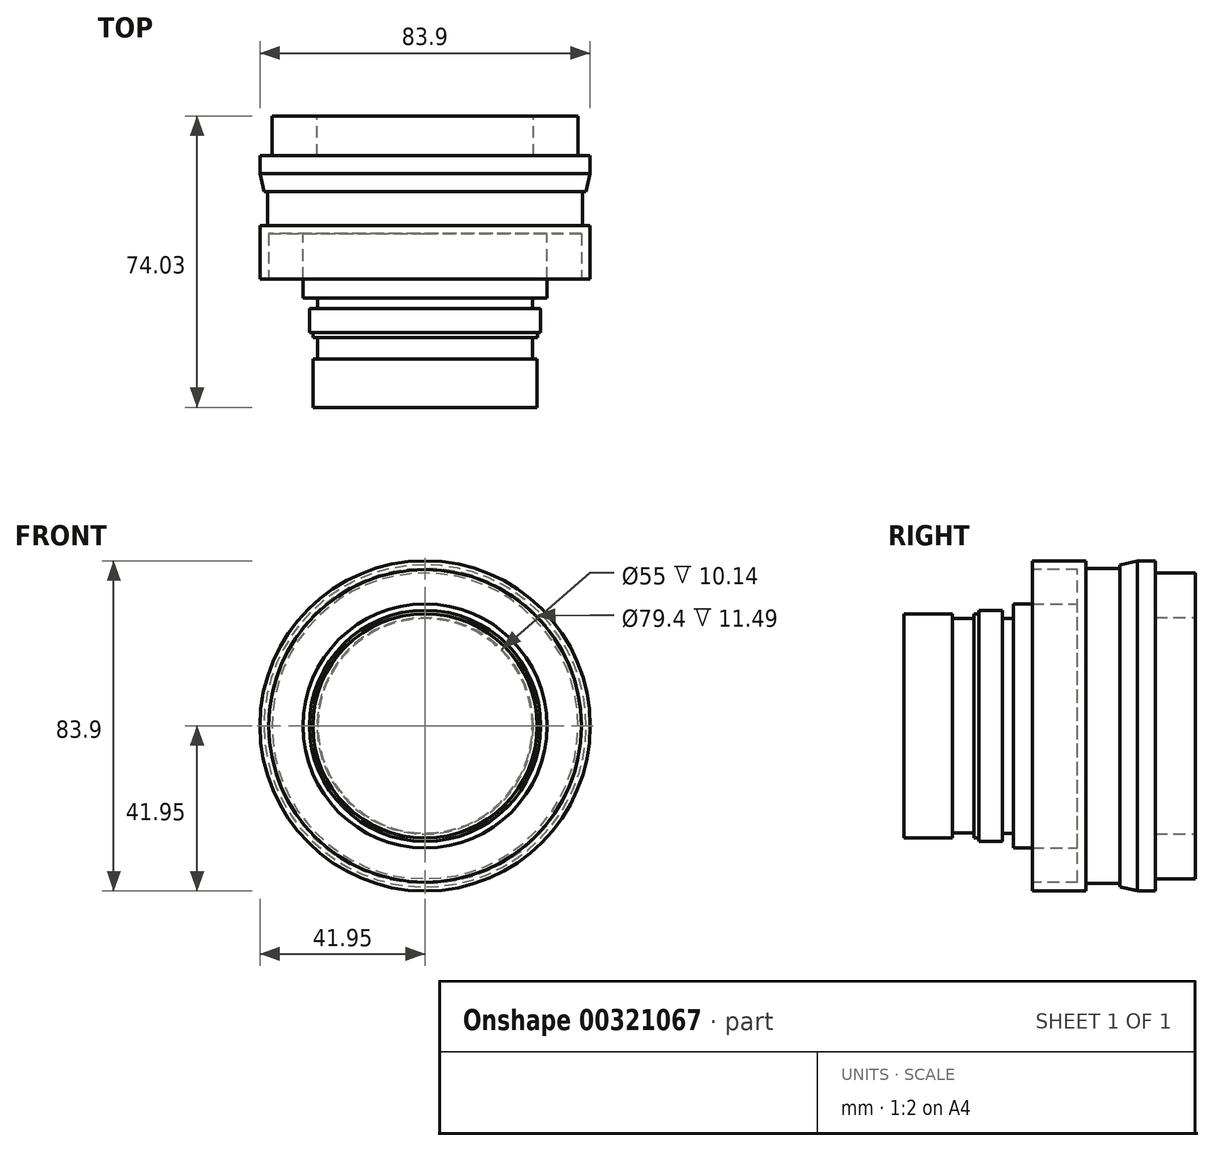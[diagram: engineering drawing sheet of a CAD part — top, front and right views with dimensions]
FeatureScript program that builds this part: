
annotation { "Feature Type Name" : "Feature", "Feature Type Description" : "" }
export const myFeature = defineFeature(function(context is Context, id is Id, definition is map)
    precondition{}
    {
        {
            var Q0;
            Q0=qCreatedBy(makeId("Front.planeOp"),FACE);
            var sketch = newSketch(context, id + "F0", { "sketchPlane" : qUnion([Q0])});
            skCircle(sketch, "E0", {"center": v(0, 0) * mm, "radius": 38.84 * mm});
            skCircle(sketch, "E1", {"center": v(0, 0) * mm, "radius": 27.5 * mm});
            skSolve(sketch);
        }
        {
            var Q0;
            Q0 = qSketchRegion(id + "F0", true);
            extrude(context, id + "F1", {"entities" : qUnion([Q0]), "depth" : 10.14 * mm});
        }
        {
            var Q0;
            Q0=makeQuery(id+"F1.opExtrude","CAP_FACE",FACE,{"disambiguationData":[OSD([sQuery(id+"F0.wireOp",EDGE,"E0"),sQuery(id+"F0.wireOp",EDGE,"E1")])],"isStart":false});
            var sketch = newSketch(context, id + "F2", { "sketchPlane" : qUnion([Q0])});
            skCircle(sketch, "E2", {"center": v(0, 0) * mm, "radius": 41.88 * mm});
            skSolve(sketch);
        }
        {
            var Q0;
            Q0 = qSketchRegion(id + "F2", true);
            extrude(context, id + "F3", {"entities" : qUnion([Q0]), "operationType" : NewBodyOperationType.ADD, "depth" : 4.57 * mm});
        }
        {
            var Q0;
            Q0=makeQuery(id+"F3.opExtrude","CAP_FACE",FACE,{"disambiguationData":[OSD([sQuery(id+"F2.wireOp",EDGE,"E2")])],"isStart":false});
            var sketch = newSketch(context, id + "F4", { "sketchPlane" : qUnion([Q0])});
            skCircle(sketch, "E3", {"center": v(0, 0) * mm, "radius": 41.88 * mm});
            skSolve(sketch);
        }
        {
            var Q0;
            Q0=makeQuery(id+"F4.imprint","IMPRINT",FACE,{"disambiguationData":[TD([[makeQuery(id+"F4.imprint","IMPRINT",EDGE,{"derivedFrom":sQuery(id+"F4.wireOp",EDGE,"E3")}),1.0]])]});
            cPlane(context, id + "F5", {"entities" : qUnion([Q0]), "cplaneType" : CPlaneType.OFFSET, "offset" : 4.5 * mm, "width" : 150 * mm, "height" : 150 * mm});
        }
        {
            var Q0;
            Q0=qCreatedBy(id+"F5.planeOp",FACE);
            var sketch = newSketch(context, id + "F6", { "sketchPlane" : qUnion([Q0])});
            skCircle(sketch, "E4", {"center": v(0, 0) * mm, "radius": 40.92 * mm});
            skSolve(sketch);
        }
        {
            var Q1;
            Q1 = qSketchRegion(id + "F4", true);
            var Q2;
            Q2 = qSketchRegion(id + "F6", true);
            loft(context, id + "F7", {"operationType" : NewBodyOperationType.ADD, "sheetProfilesArray" : [{ "sheetProfileEntities" : qUnion([Q1]) }, { "sheetProfileEntities" : qUnion([Q2]) }]});
        }
        {
            var Q0;
            Q0=makeQuery(id+"F7.opLoft","CAP_FACE",FACE,{"disambiguationData":[OSD([makeQuery(id+"F6.imprint","IMPRINT",FACE,{"disambiguationData":[TD([[makeQuery(id+"F6.imprint","IMPRINT",EDGE,{"derivedFrom":sQuery(id+"F6.wireOp",EDGE,"E4")}),1.0]])]})])],"isStart":true});
            var sketch = newSketch(context, id + "F8", { "sketchPlane" : qUnion([Q0])});
            skCircle(sketch, "E5", {"center": v(0, 0) * mm, "radius": 40 * mm});
            skSolve(sketch);
        }
        {
            var Q0;
            Q0 = qSketchRegion(id + "F8", true);
            extrude(context, id + "F9", {"entities" : qUnion([Q0]), "operationType" : NewBodyOperationType.ADD, "depth" : 8.65 * mm});
        }
        {
            var Q0;
            Q0=makeQuery(id+"F9.opExtrude","CAP_FACE",FACE,{"disambiguationData":[OSD([sQuery(id+"F8.wireOp",EDGE,"E5")])],"isStart":false});
            var sketch = newSketch(context, id + "F10", { "sketchPlane" : qUnion([Q0])});
            skCircle(sketch, "E6", {"center": v(0, 0) * mm, "radius": 41.95 * mm});
            skSolve(sketch);
        }
        {
            var Q0;
            Q0 = qSketchRegion(id + "F10", true);
            extrude(context, id + "F11", {"entities" : qUnion([Q0]), "operationType" : NewBodyOperationType.ADD, "depth" : 13.57 * mm});
        }
        {
            var Q0;
            Q0=makeQuery(id+"F11.opExtrude","CAP_FACE",FACE,{"disambiguationData":[OSD([sQuery(id+"F10.wireOp",EDGE,"E6")])],"isStart":false});
            var sketch = newSketch(context, id + "F12", { "sketchPlane" : qUnion([Q0])});
            skCircle(sketch, "E7", {"center": v(0, 0) * mm, "radius": 39.7 * mm});
            skSolve(sketch);
        }
        {
            var Q0;
            Q0 = qSketchRegion(id + "F12", true);
            extrude(context, id + "F13", {"entities" : qUnion([Q0]), "operationType" : NewBodyOperationType.REMOVE, "oppositeDirection" : true, "depth" : 11.5 * mm});
        }
        {
            var Q0;
            Q0=makeQuery(id+"F13.boolean.opBoolean","COPY",FACE,{"derivedFrom":makeQuery(id+"F13.opExtrude","CAP_FACE",FACE,{"disambiguationData":[OSD([sQuery(id+"F12.wireOp",EDGE,"E7")])],"isStart":false})});
            var sketch = newSketch(context, id + "F14", { "sketchPlane" : qUnion([Q0])});
            skCircle(sketch, "E8", {"center": v(0, 0) * mm, "radius": 31 * mm});
            skSolve(sketch);
        }
        {
            var Q0;
            Q0 = qSketchRegion(id + "F14", true);
            extrude(context, id + "F15", {"entities" : qUnion([Q0]), "operationType" : NewBodyOperationType.ADD, "depth" : 16.29 * mm});
        }
        {
            var Q0;
            Q0=makeQuery(id+"F15.opExtrude","CAP_FACE",FACE,{"disambiguationData":[OSD([sQuery(id+"F14.wireOp",EDGE,"E8")])],"isStart":false});
            var sketch = newSketch(context, id + "F16", { "sketchPlane" : qUnion([Q0])});
            skCircle(sketch, "E9", {"center": v(0, 0) * mm, "radius": 27.3 * mm});
            skSolve(sketch);
        }
        {
            var Q0;
            Q0 = qSketchRegion(id + "F16", true);
            extrude(context, id + "F17", {"entities" : qUnion([Q0]), "operationType" : NewBodyOperationType.ADD, "depth" : 2.75 * mm});
        }
        {
            var Q0;
            Q0=makeQuery(id+"F17.opExtrude","CAP_FACE",FACE,{"disambiguationData":[OSD([sQuery(id+"F16.wireOp",EDGE,"E9")])],"isStart":false});
            var sketch = newSketch(context, id + "F18", { "sketchPlane" : qUnion([Q0])});
            skCircle(sketch, "E10", {"center": v(0, 0) * mm, "radius": 29.38 * mm});
            skSolve(sketch);
        }
        {
            var Q0;
            Q0 = qSketchRegion(id + "F18", true);
            extrude(context, id + "F19", {"entities" : qUnion([Q0]), "operationType" : NewBodyOperationType.ADD, "depth" : 6 * mm});
        }
        {
            var Q0;
            Q0=makeQuery(id+"F19.opExtrude","CAP_FACE",FACE,{"disambiguationData":[OSD([sQuery(id+"F18.wireOp",EDGE,"E10")])],"isStart":false});
            var sketch = newSketch(context, id + "F20", { "sketchPlane" : qUnion([Q0])});
            skCircle(sketch, "E11", {"center": v(0, 0) * mm, "radius": 28.5 * mm});
            skSolve(sketch);
        }
        {
            var Q0;
            Q0 = qSketchRegion(id + "F20", true);
            extrude(context, id + "F21", {"entities" : qUnion([Q0]), "operationType" : NewBodyOperationType.ADD, "depth" : 1.3 * mm});
        }
        {
            var Q0;
            Q0=makeQuery(id+"F21.opExtrude","CAP_FACE",FACE,{"disambiguationData":[OSD([sQuery(id+"F20.wireOp",EDGE,"E11")])],"isStart":false});
            var sketch = newSketch(context, id + "F22", { "sketchPlane" : qUnion([Q0])});
            skCircle(sketch, "E12", {"center": v(0, 0) * mm, "radius": 27.25 * mm});
            skSolve(sketch);
        }
        {
            var Q0;
            Q0 = qSketchRegion(id + "F22", true);
            extrude(context, id + "F23", {"entities" : qUnion([Q0]), "operationType" : NewBodyOperationType.ADD, "depth" : 5.5 * mm});
        }
        {
            var Q0;
            Q0=makeQuery(id+"F23.opExtrude","CAP_FACE",FACE,{"disambiguationData":[OSD([sQuery(id+"F22.wireOp",EDGE,"E12")])],"isStart":false});
            var sketch = newSketch(context, id + "F24", { "sketchPlane" : qUnion([Q0])});
            skCircle(sketch, "E13", {"center": v(0, 0) * mm, "radius": 28.48 * mm});
            skSolve(sketch);
        }
        {
            var Q0;
            Q0 = qSketchRegion(id + "F24", true);
            extrude(context, id + "F25", {"entities" : qUnion([Q0]), "operationType" : NewBodyOperationType.ADD, "depth" : 12.25 * mm});
        }
    });
